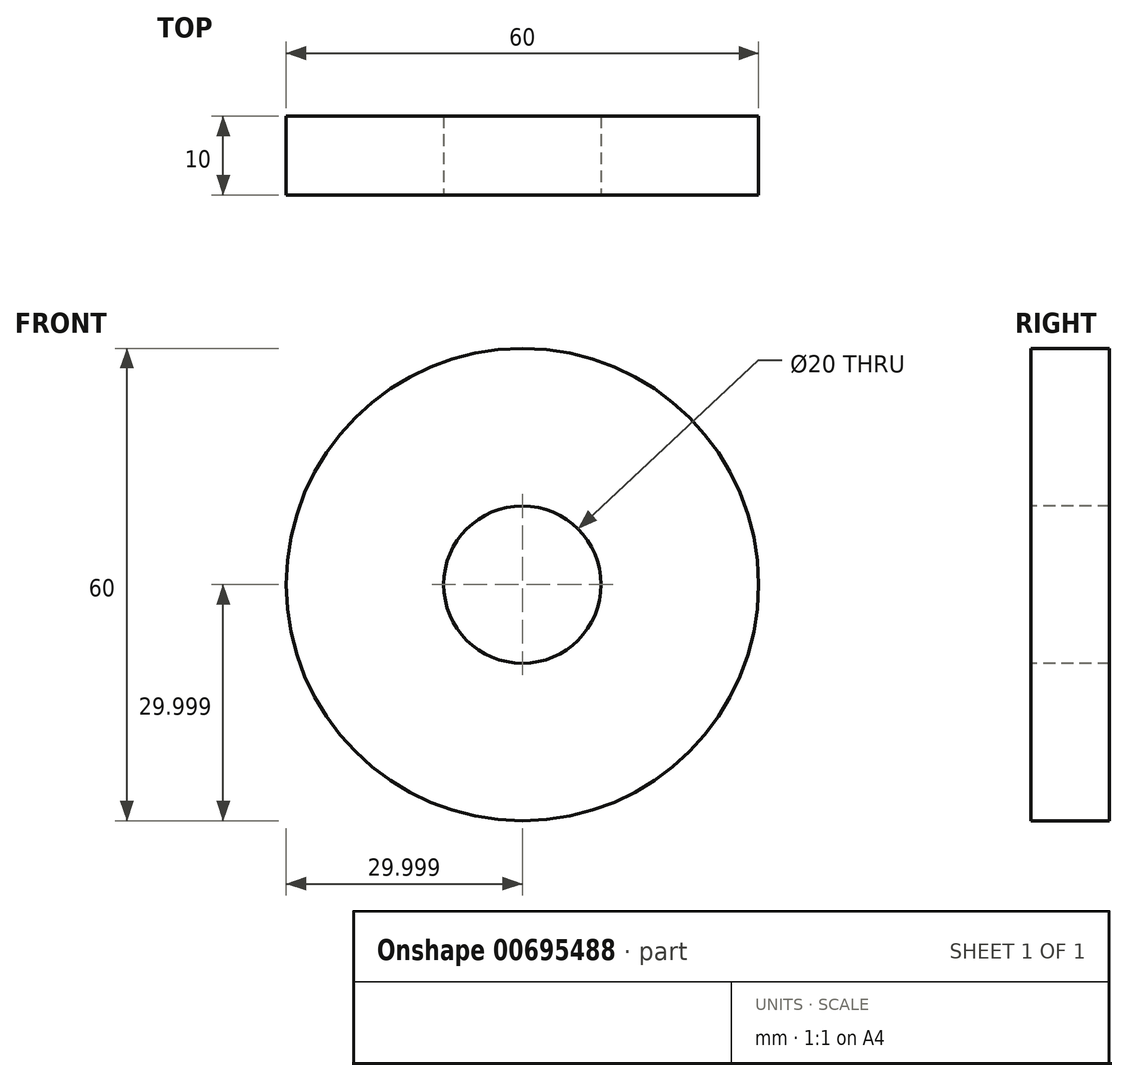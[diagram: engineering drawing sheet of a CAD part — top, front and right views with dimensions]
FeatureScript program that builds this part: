
annotation { "Feature Type Name" : "Feature", "Feature Type Description" : "" }
export const myFeature = defineFeature(function(context is Context, id is Id, definition is map)
    precondition{}
    {
        {
            var Q0;
            Q0=qCreatedBy(makeId("Front.planeOp"),FACE);
            var sketch = newSketch(context, id + "F0", { "sketchPlane" : qUnion([Q0])});
            skCircle(sketch, "E0", {"center": v(12.7, 30.99) * mm, "radius": 30 * mm});
            skSolve(sketch);
        }
        {
            var Q0;
            Q0 = qSketchRegion(id + "F0", true);
            extrude(context, id + "F1", {"entities" : qUnion([Q0]), "depth" : 10 * mm, "offsetDistance" : 25 * mm});
        }
        {
            var Q0;
            Q0=makeQuery(id+"F1.opExtrude","CAP_FACE",FACE,{"disambiguationData":[OSD([sQuery(id+"F0.wireOp",EDGE,"E0")])],"isStart":false});
            var sketch = newSketch(context, id + "F2", { "sketchPlane" : qUnion([Q0])});
            skPoint(sketch, "E1.0", {"position": v(12.7, 30.99) * mm});
            skSolve(sketch);
        }
        {
            var Q0;
            Q0=sQuery(id+"F2.wireOp",VERTEX,"E1.0");
            var Q1;
            Q1=makeQuery(id+"F1.opExtrude","SWEPT_BODY",BODY,{"disambiguationData":[OSD([sQuery(id+"F0.wireOp",EDGE,"E0")])]});
            hole(context, id + "F3", {"style" : HoleStyle.SIMPLE, "endStyle" : HoleEndStyle.THROUGH, "holeDiameter" : 20 * mm, "majorDiameter" : 5 * mm, "isTappedThrough" : true, "tappedDepth" : 12 * mm, "tapClearance" : 3, "locations" : qUnion([Q0]), "scope" : qUnion([Q1])});
        }
    });
